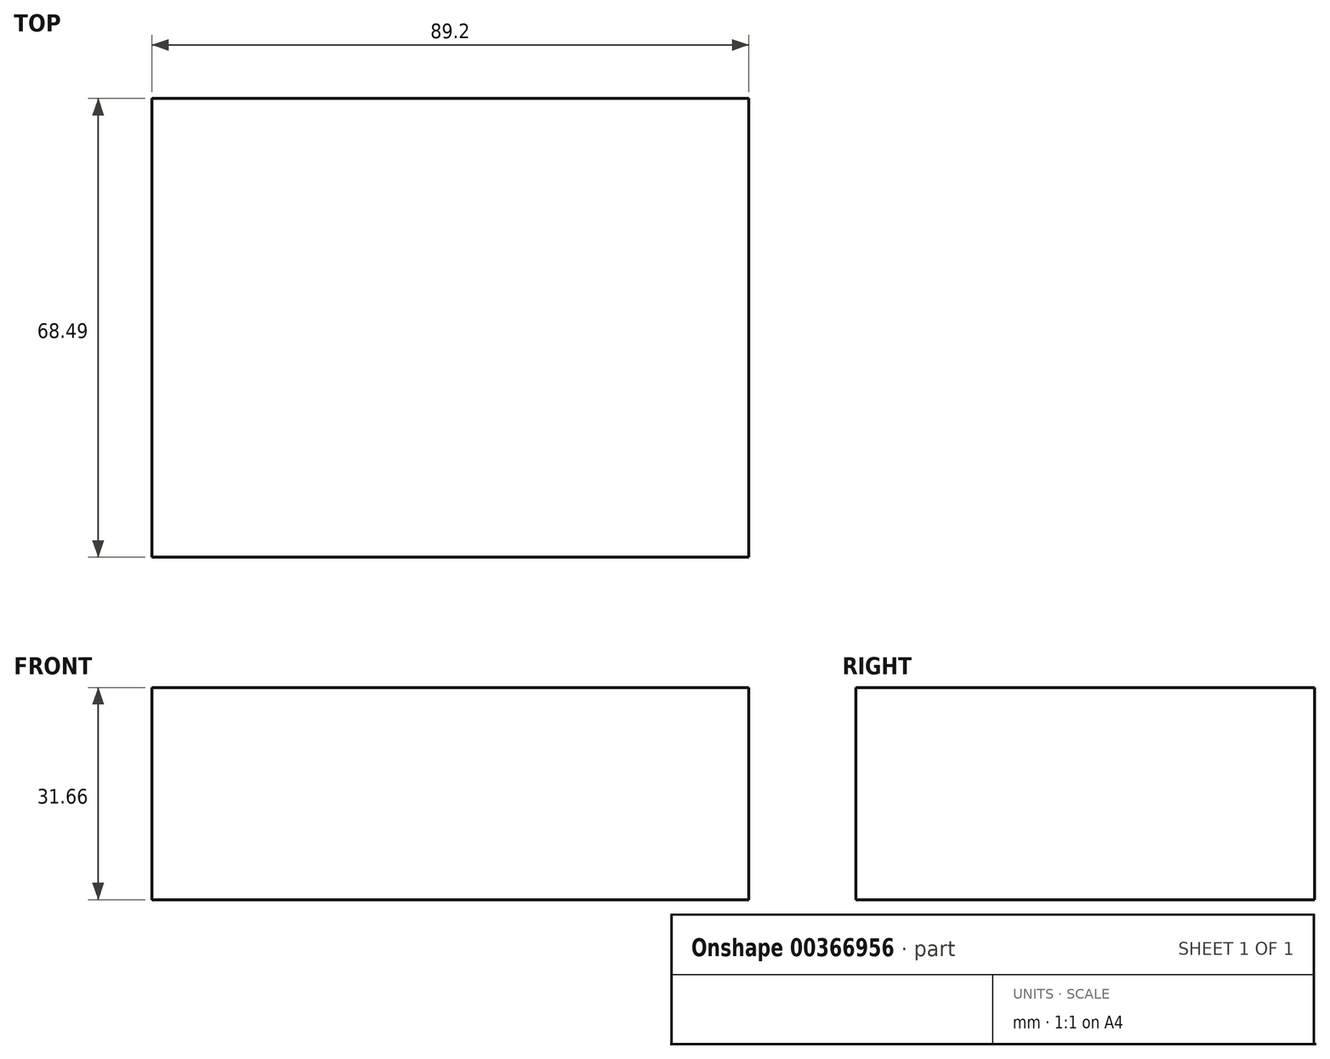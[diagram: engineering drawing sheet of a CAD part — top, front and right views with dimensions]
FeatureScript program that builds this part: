
annotation { "Feature Type Name" : "Feature", "Feature Type Description" : "" }
export const myFeature = defineFeature(function(context is Context, id is Id, definition is map)
    precondition{}
    {
        {
            var Q0;
            Q0=qCreatedBy(makeId("Top.planeOp"),FACE);
            var sketch = newSketch(context, id + "F0", { "sketchPlane" : qUnion([Q0])});
            skLineSegment(sketch, "E0.bottom", {"start": v(44.6, 0) * mm, "end": v(-44.6, 0) * mm});
            skLineSegment(sketch, "E0.top", {"start": v(44.6, -68.49) * mm, "end": v(-44.6, -68.49) * mm});
            skLineSegment(sketch, "E0.left", {"start": v(44.6, 0) * mm, "end": v(44.6, -68.49) * mm});
            skLineSegment(sketch, "E0.right", {"start": v(-44.6, 0) * mm, "end": v(-44.6, -68.49) * mm});
            skPoint(sketch, "E0.middle", {"position": v(0, -34.24) * mm});
            skSolve(sketch);
        }
        {
            var Q0;
            Q0 = qSketchRegion(id + "F0", true);
            extrude(context, id + "F1", {"entities" : qUnion([Q0]), "oppositeDirection" : true, "depth" : 31.66 * mm});
        }
    });
